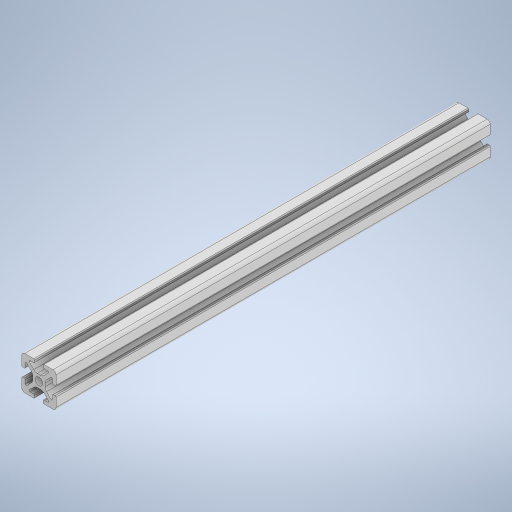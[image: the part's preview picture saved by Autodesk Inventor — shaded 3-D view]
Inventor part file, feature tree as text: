
AUTODESK INVENTOR PART (.ipt)
format: ipt  version: 2023 (Build 270158000, 158)  size: 418,816 bytes
history: mixed  units: in
note: dims shown in document units (in); Inventor stores cm internally (conversion verified against a paired STEP export)
features: extrude x1, sketch x1, projected_geometry x1, mirror x1, imported_body x1
ambient origin geometry x8: Origin, YZ Plane, XZ Plane, XY Plane, X Axis, Y Axis, Z Axis, Center Point
bodies: Solid1 (imported_parasolid)
feature tree (5):
  extrude  "Extrusion1"  [1 undecoded]
  sketch  "Sketch1"  dims[d0=2.0in d1=0.0in]
  projected_geometry  "Projected Loop1"
  mirror  "Mirror2"
  imported_body  NMx_Import_Brep_tag  [imported B-rep: ~75 faces, bbox_mm=[20.0, 20.0, 254.0]]
note: 1 required parameter value undecoded (feature->parameter linkage not recoverable at this tier; creation-order binding heuristic only, values carry confidence <= 0.55)
